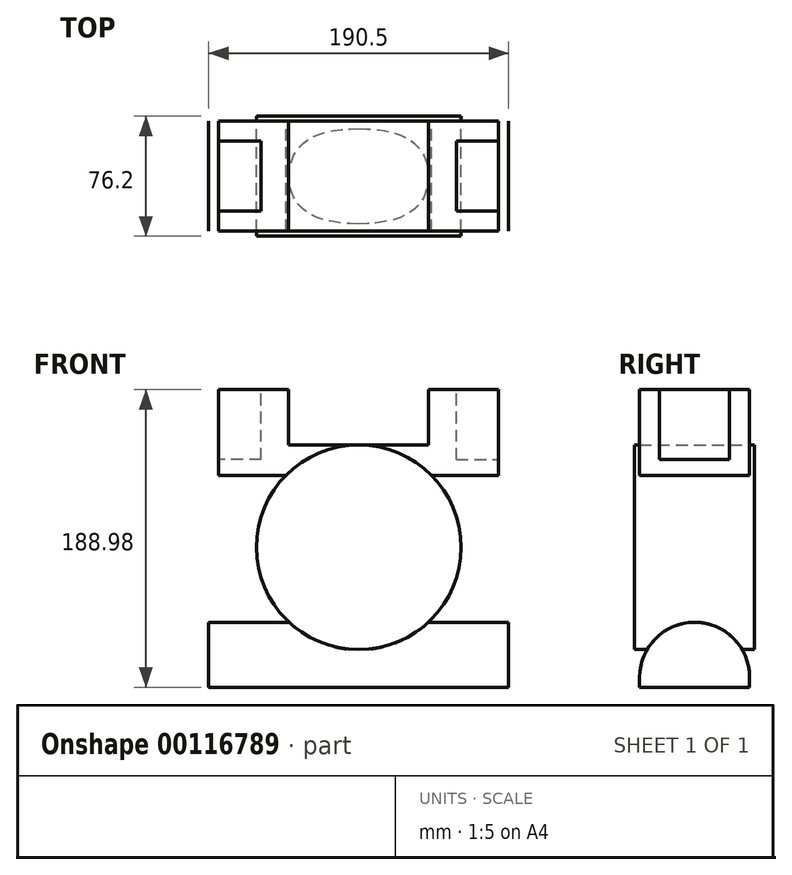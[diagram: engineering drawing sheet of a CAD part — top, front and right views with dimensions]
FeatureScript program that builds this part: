
annotation { "Feature Type Name" : "Feature", "Feature Type Description" : "" }
export const myFeature = defineFeature(function(context is Context, id is Id, definition is map)
    precondition{}
    {
        {
            var Q0;
            Q0=qCreatedBy(makeId("Front.planeOp"),FACE);
            var sketch = newSketch(context, id + "F0", { "sketchPlane" : qUnion([Q0])});
            skCircle(sketch, "E0", {"center": v(0, 0) * mm, "radius": 65.02 * mm});
            skSolve(sketch);
        }
        {
            var Q0;
            Q0=makeQuery(id+"F0.imprint","IMPRINT",FACE,{"disambiguationData":[TD([[makeQuery(id+"F0.imprint","IMPRINT",EDGE,{"derivedFrom":sQuery(id+"F0.wireOp",EDGE,"E0")}),1.0]])]});
            extrude(context, id + "F1", {"entities" : qUnion([Q0]), "endBound" : BoundingType.SYMMETRIC, "depth" : 76.2 * mm});
        }
        {
            var Q0;
            Q0=qCreatedBy(makeId("Right.planeOp"),FACE);
            var sketch = newSketch(context, id + "F2", { "sketchPlane" : qUnion([Q0])});
            skLineSegment(sketch, "E1", {"start": v(0, 0) * mm, "end": v(0, -82.55) * mm});
            skArc(sketch, "E2", {"start": v(34.93, -82.55) * mm, "mid": v(0, -47.63) * mm, "end": v(-34.93, -82.55) * mm});
            skLineSegment(sketch, "E3", {"start": v(-34.93, -88.9) * mm, "end": v(34.93, -88.9) * mm});
            skLineSegment(sketch, "E4", {"start": v(-34.93, -82.55) * mm, "end": v(-34.93, -88.9) * mm});
            skLineSegment(sketch, "E5.MirrorCS", {"start": v(34.93, -82.55) * mm, "end": v(34.93, -88.9) * mm});
            skPoint(sketch, "E6.orphan", {"position": v(-34.93, -136.52) * mm});
            skPoint(sketch, "E7.orphan", {"position": v(34.93, -136.52) * mm});
            skSolve(sketch);
        }
        {
            var Q0;
            Q0=makeQuery(id+"F2.imprint","IMPRINT",FACE,{"disambiguationData":[TD([[makeQuery(id+"F2.imprint","IMPRINT",EDGE,{"derivedFrom":sQuery(id+"F2.wireOp",EDGE,"E2")}),1.0]])]});
            extrude(context, id + "F3", {"entities" : qUnion([Q0]), "operationType" : NewBodyOperationType.ADD, "endBound" : BoundingType.SYMMETRIC, "depth" : 190.5 * mm});
        }
        {
            var Q0;
            Q0=qCreatedBy(makeId("Front.planeOp"),FACE);
            var sketch = newSketch(context, id + "F4", { "sketchPlane" : qUnion([Q0])});
            skLineSegment(sketch, "E8", {"start": v(0, 0) * mm, "end": v(0, 65.02) * mm});
            skLineSegment(sketch, "E9.bottom", {"start": v(-88.9, 100.08) * mm, "end": v(-44.45, 100.08) * mm});
            skLineSegment(sketch, "E9.top", {"start": v(-88.9, 45.72) * mm, "end": v(88.9, 45.72) * mm});
            skLineSegment(sketch, "E9.left", {"start": v(-88.9, 100.08) * mm, "end": v(-88.9, 45.72) * mm});
            skLineSegment(sketch, "E9.right", {"start": v(88.9, 100.08) * mm, "end": v(88.9, 45.72) * mm});
            skPoint(sketch, "E10", {"position": v(44.45, 100.08) * mm});
            skLineSegment(sketch, "E11", {"start": v(0, 65.02) * mm, "end": v(44.45, 65.02) * mm});
            skLineSegment(sketch, "E12", {"start": v(44.45, 100.08) * mm, "end": v(44.45, 65.02) * mm});
            skLineSegment(sketch, "E13.MirrorCS", {"start": v(88.9, 65.02) * mm, "end": v(44.45, 65.02) * mm});
            skLineSegment(sketch, "E14.MirrorCS", {"start": v(0, 65.02) * mm, "end": v(-44.45, 65.02) * mm});
            skLineSegment(sketch, "E15.MirrorCS", {"start": v(-44.45, 100.08) * mm, "end": v(-44.45, 65.02) * mm});
            skLineSegment(sketch, "E16.trimOffspring", {"start": v(44.45, 100.08) * mm, "end": v(88.9, 100.08) * mm});
            skSolve(sketch);
        }
        {
            var Q0;
            Q0=makeQuery(id+"F4.imprint","IMPRINT",FACE,{"disambiguationData":[TD([[makeQuery(id+"F4.imprint","IMPRINT",EDGE,{"derivedFrom":sQuery(id+"F4.wireOp",EDGE,"E9.bottom")}),-1.0]])]});
            var Q1;
            Q1=makeQuery(id+"F4.imprint","IMPRINT",FACE,{"disambiguationData":[TD([[makeQuery(id+"F4.imprint","IMPRINT",EDGE,{"derivedFrom":sQuery(id+"F4.wireOp",EDGE,"E12")}),1.0]])]});
            var Q2;
            {var subQ0=sQuery(id+"F4.wireOp",EDGE,"E11");Q2=makeQuery(id+"F4.imprint","IMPRINT",FACE,{"disambiguationData":[TD([[makeQuery(id+"F4.imprint","IMPRINT",EDGE,{"derivedFrom":subQ0}),-1.0]])]});}
            extrude(context, id + "F5", {"entities" : qUnion([Q0, Q1, Q2]), "operationType" : NewBodyOperationType.ADD, "endBound" : BoundingType.SYMMETRIC, "depth" : 69.85 * mm});
        }
        {
            var Q0;
            Q0=makeQuery(id+"F5.opExtrude","SWEPT_FACE",FACE,{"disambiguationData":[OSD([sQuery(id+"F4.wireOp",EDGE,"E16.trimOffspring")])]});
            var sketch = newSketch(context, id + "F6", { "sketchPlane" : qUnion([Q0])});
            skLineSegment(sketch, "E17", {"start": v(0, 0) * mm, "end": v(142.83, 0) * mm});
            skLineSegment(sketch, "E18.bottom", {"start": v(61.98, -22.23) * mm, "end": v(119.5, -22.23) * mm});
            skLineSegment(sketch, "E18.top", {"start": v(61.98, 22.23) * mm, "end": v(119.5, 22.23) * mm});
            skLineSegment(sketch, "E18.left", {"start": v(61.98, -22.23) * mm, "end": v(61.98, 22.23) * mm});
            skLineSegment(sketch, "E18.right", {"start": v(119.5, -22.23) * mm, "end": v(119.5, 22.23) * mm});
            skLineSegment(sketch, "E19.MirrorCS", {"start": v(-61.98, -22.23) * mm, "end": v(-119.5, -22.23) * mm});
            skLineSegment(sketch, "E20.MirrorCS", {"start": v(-61.98, -22.23) * mm, "end": v(-61.98, 22.23) * mm});
            skLineSegment(sketch, "E21.MirrorCS", {"start": v(-61.98, 22.23) * mm, "end": v(-119.5, 22.23) * mm});
            skLineSegment(sketch, "E22.MirrorCS", {"start": v(-119.5, -22.23) * mm, "end": v(-119.5, 22.23) * mm});
            skSolve(sketch);
        }
        {
            var Q0;
            Q0=makeQuery(id+"F6.imprint","IMPRINT",FACE,{"disambiguationData":[TD([[makeQuery(id+"F6.imprint","IMPRINT",EDGE,{"derivedFrom":sQuery(id+"F6.wireOp",EDGE,"E19.MirrorCS")}),-1.0]])]});
            var Q1;
            {var subQ0=sQuery(id+"F6.wireOp",EDGE,"E18.left");var subQ5=sQuery(id+"F6.wireOp",EDGE,"E18.bottom");var subQ6=makeQuery(id+"F6.imprint","INTERSECT",VERTEX,{"derivedFrom":[subQ5,subQ0]});Q1=makeQuery(id+"F6.imprint","IMPRINT",FACE,{"disambiguationData":[TD([[makeQuery(id+"F6.imprint","IMPRINT",EDGE,{"disambiguationData":[TD([[subQ6,-1.0]])],"derivedFrom":subQ0}),-1.0]])]});}
            var Q2;
            {var subQ0=sQuery(id+"F6.wireOp",EDGE,"E18.left");var subQ5=sQuery(id+"F6.wireOp",EDGE,"E18.top");var subQ6=makeQuery(id+"F6.imprint","INTERSECT",VERTEX,{"derivedFrom":[subQ5,subQ0]});Q2=makeQuery(id+"F6.imprint","IMPRINT",FACE,{"disambiguationData":[TD([[makeQuery(id+"F6.imprint","IMPRINT",EDGE,{"disambiguationData":[TD([[subQ6,1.0]])],"derivedFrom":subQ0}),-1.0]])]});}
            extrude(context, id + "F7", {"entities" : qUnion([Q0, Q1, Q2]), "operationType" : NewBodyOperationType.REMOVE, "oppositeDirection" : true, "depth" : 44.45 * mm});
        }
    });
